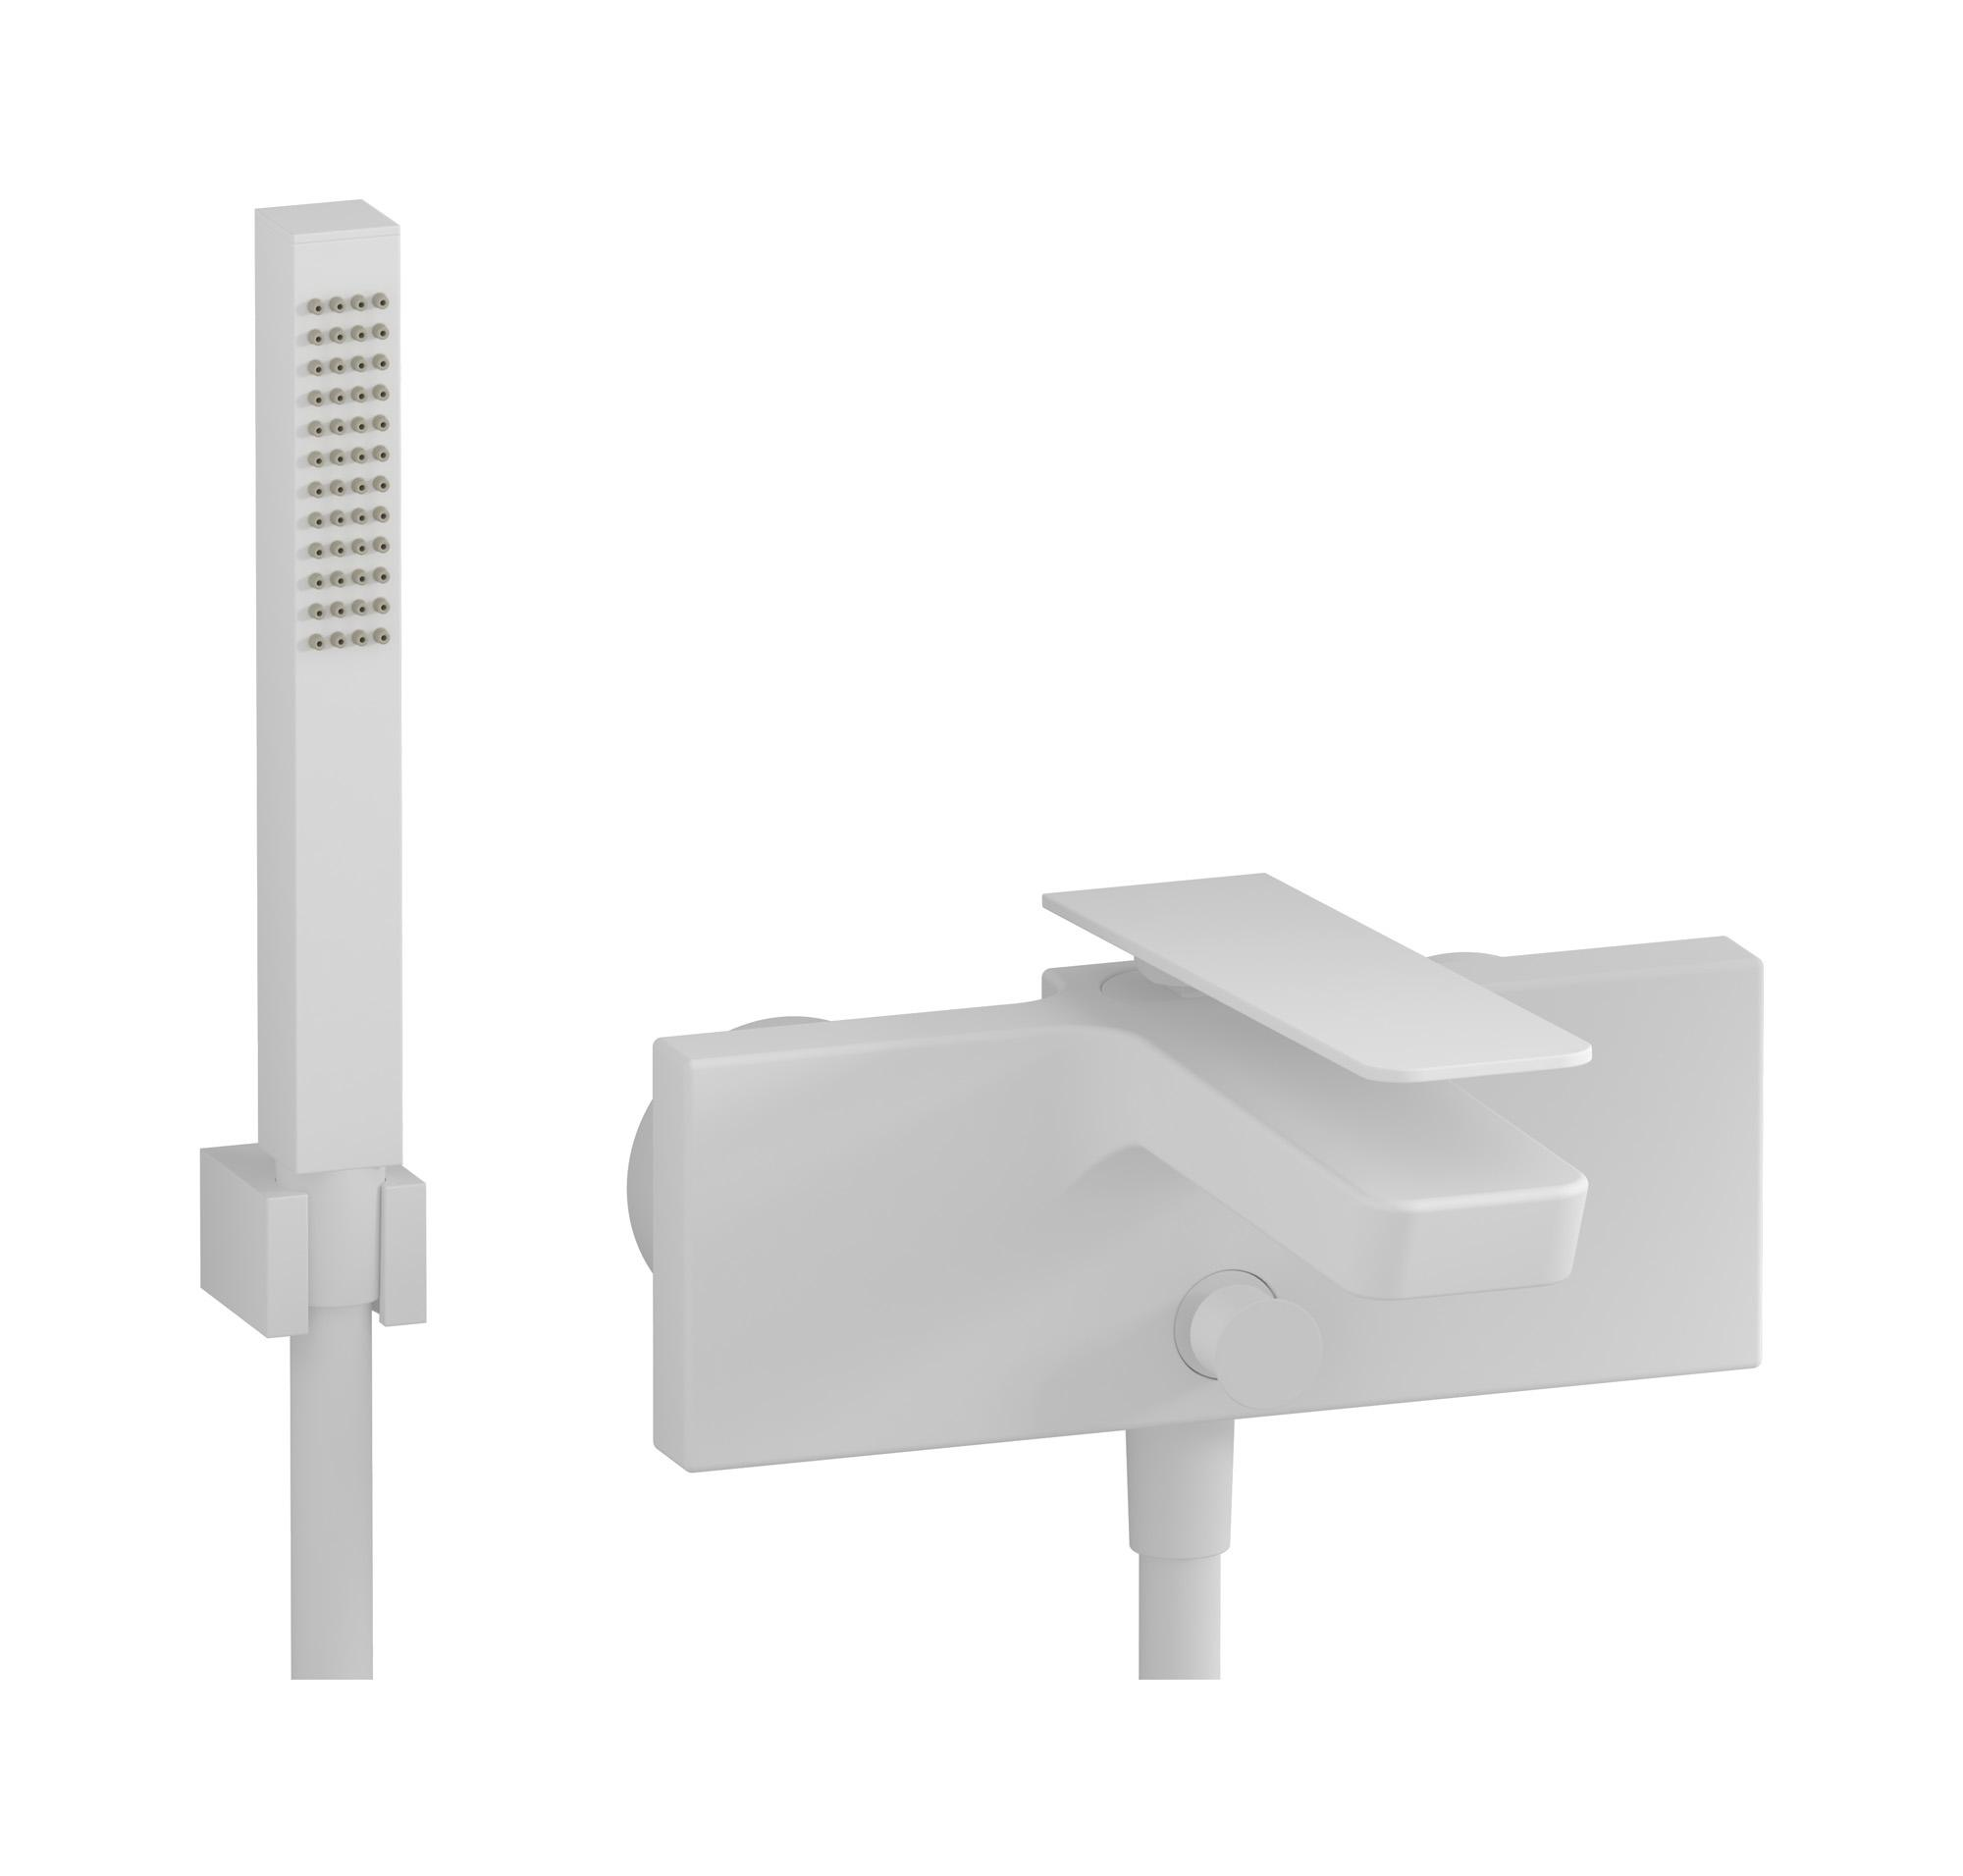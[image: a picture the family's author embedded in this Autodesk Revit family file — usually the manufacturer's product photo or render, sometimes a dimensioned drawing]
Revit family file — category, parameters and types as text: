
# Revit family: K3250
name_source: partatom
category: Apparecchi idraulici
units: mm (PartAtom-declared; Revit-internal decimal feet)

## family parameters
Basato su piano di lavoro = No
Condiviso = No
Mantieni orientamento annotazione = No
Numero OmniClass = 23.45.55.17
Punto di calcolo locali = No
Quota connettore circolare = Usa diametro
Sempre verticale = Sì
Taglio con vuoti quando caricato = No
Tipo di parte = Normale
Titolo OmniClass = Mixing Faucets

## types (8) — shared parameters
Cold water inlet = 10 mm  [stored 0.0328084 ft]
Commenti sul tipo = Bath filler
Connessione CW = No
Connessione HW = No
Connessione di scarico = No
Connessione di ventilazione = No
Descrizione = Wall mounted bath filler complete with shower kit
Hot water inlet = 10 mm  [stored 0.0328084 ft]
Produttore = IB Rubinetterie S.p.A.
URL = https://www.weareib.it
zero-valued in all types: Prospetto di default

## per-type parameters (varying)
| type | Finishes surface | Immagine tipo | Modello |
| Chrome | IB_Chrome | K3250CC.jpg | K3250CC |
| Brushed nickel | IB_Brushed nickel | K3250SS.jpg | K3250SS |
| Matt black | IB_matt black | K3250NP.jpg | K3250NP |
| Matt white | IB_matt white | K3250BO.jpg | K3250BO |
| Pale gold | IB_Pale gold | K3250II.jpg | K3250II |
| Brushed pale gold | IB_brushed pale gold | K3250IS.jpg | K3250IS |
| Rose gold | IB_Rose gold | K3250RS.jpg | K3250RS |
| Gold | IB_gold | K3250OO.jpg | K3250OO |

note: [stored X ft] marks values corroborated as IEEE doubles in the binary element streams (Revit-internal decimal feet)
